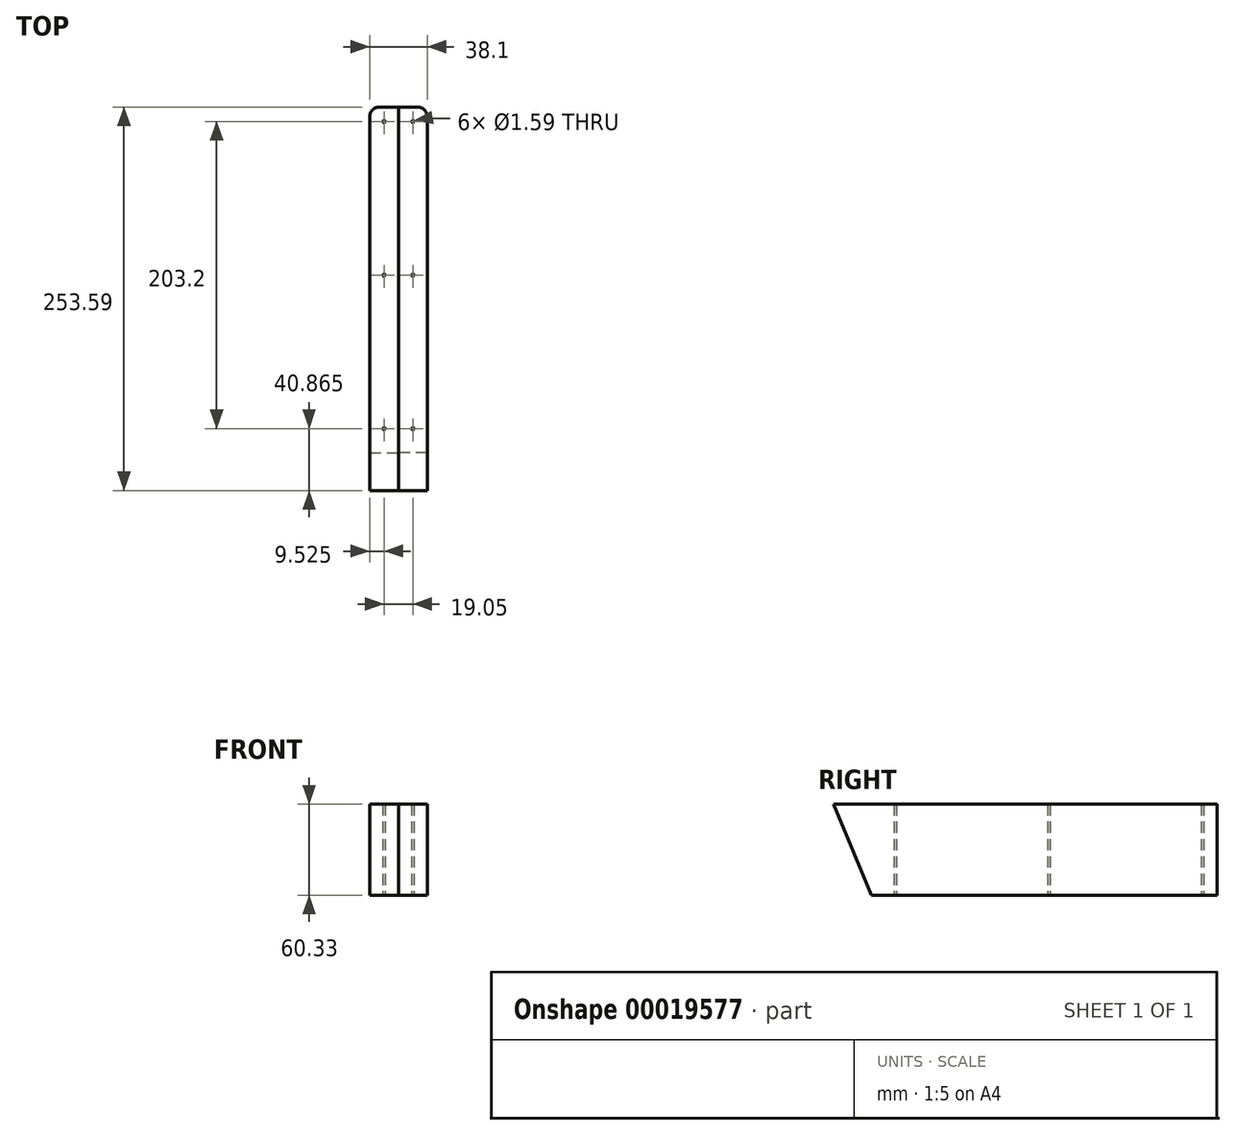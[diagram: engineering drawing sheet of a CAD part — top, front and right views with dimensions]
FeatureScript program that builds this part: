
annotation { "Feature Type Name" : "Feature", "Feature Type Description" : "" }
export const myFeature = defineFeature(function(context is Context, id is Id, definition is map)
    precondition{}
    {
        {
            var Q0;
            Q0=qCreatedBy(makeId("Right.planeOp"),FACE);
            var sketch = newSketch(context, id + "F0", { "sketchPlane" : qUnion([Q0])});
            skLineSegment(sketch, "E0", {"start": v(0, 0) * mm, "end": v(0, 60.33) * mm});
            skLineSegment(sketch, "E1", {"start": v(0, 60.33) * mm, "end": v(-253.59, 60.32) * mm});
            skLineSegment(sketch, "E2", {"start": v(-253.59, 60.32) * mm, "end": v(-228.6, 0) * mm});
            skLineSegment(sketch, "E3", {"start": v(-228.6, 0) * mm, "end": v(0, 0) * mm});
            skLineSegment(sketch, "E4", {"start": v(-228.6, 0) * mm, "end": v(-228.6, 60.32) * mm, "construction": true});
            skSolve(sketch);
        }
        {
            var Q0;
            Q0=makeQuery(id+"F0.imprint","IMPRINT",FACE,{"disambiguationData":[TD([[makeQuery(id+"F0.imprint","IMPRINT",EDGE,{"derivedFrom":sQuery(id+"F0.wireOp",EDGE,"E0")}),1.0]])]});
            extrude(context, id + "F1", {"entities" : qUnion([Q0]), "depth" : 19.05 * mm});
        }
        {
            var Q0;
            Q0=makeQuery(id+"F1.opExtrude","CAP_EDGE",EDGE,{"disambiguationData":[OSD([sQuery(id+"F0.wireOp",EDGE,"E0")])],"isStart":false});
            fillet(context, id + "F2", {"entities" : qUnion([Q0]), "radius" : 6.35 * mm, "tangentPropagation" : true, "allowEdgeOverflow" : false});
        }
        {
            var Q0;
            Q0=makeQuery(id+"F1.opExtrude","SWEPT_FACE",FACE,{"disambiguationData":[OSD([sQuery(id+"F0.wireOp",EDGE,"E3")])]});
            var sketch = newSketch(context, id + "F3", { "sketchPlane" : qUnion([Q0])});
            skCircle(sketch, "E5", {"center": v(9.53, 9.53) * mm, "radius": 0.8 * mm});
            skCircle(sketch, "E6", {"center": v(9.53, 111.13) * mm, "radius": 0.8 * mm});
            skCircle(sketch, "E7", {"center": v(9.53, 212.72) * mm, "radius": 0.8 * mm});
            skLineSegment(sketch, "E8", {"start": v(9.53, 9.53) * mm, "end": v(9.53, 212.72) * mm});
            skLineSegment(sketch, "E9", {"start": v(9.53, 212.72) * mm, "end": v(9.53, 228.6) * mm});
            skSolve(sketch);
        }
        {
            var Q0;
            Q0 = qSketchRegion(id + "F3", true);
            extrude(context, id + "F4", {"entities" : qUnion([Q0]), "operationType" : NewBodyOperationType.REMOVE, "endBound" : BoundingType.THROUGH_ALL, "oppositeDirection" : true, "depth" : 25.4 * mm});
        }
        {
            var Q0;
            Q0=makeQuery(id+"F1.opExtrude","SWEPT_BODY",BODY,{"disambiguationData":[OSD([sQuery(id+"F0.wireOp",EDGE,"E0"),sQuery(id+"F0.wireOp",EDGE,"E1"),sQuery(id+"F0.wireOp",EDGE,"E2"),sQuery(id+"F0.wireOp",EDGE,"E3")])]});
            var Q1;
            Q1=qCreatedBy(makeId("Right.planeOp"),FACE);
            mirror(context, id + "F5", {"entities" : qUnion([Q0]), "mirrorPlane" : qUnion([Q1])});
        }
    });
